# Revit family: HV1 für Kältefestpunkt_
name_source: partatom
category: Allgemeines Modell
revit_build: Autodesk Revit 2017 (Build: 20190508_0315(x64)
units: mm (PartAtom-declared; Revit-internal decimal feet)

## family parameters
Basisbauteil = Fläche
Beim Laden mit Abzugskörper schneiden = Nein
Bemaßung runder Anschluss = Durchmesser verwenden
Gemeinsam genutzt = Ja
Kann Basisbauteil für Bewehrung sein = Nein
Raumberechnungspunkt = Nein
Teiletyp = Normal

## types (5) — shared parameters
Anzahl Rohrschellen = 2
Anzugsmoment Hammersperrkopf = 120 Nm
Artikelnummer = 00200405/fvz
Breite Material Rohrschelle = 50 mm
EAN = 4250928400000
Fabrikat = MEFA
Gewicht = 3.58 kg
Kurztext1 = Festpunkthalterung HV 1
Kurztext2 = 64 - 273 mm Fx 20 kN 111 - 163 mm
Länge = 120 mm  [stored 0.393701 ft]
Mengeneinheit = St
Rohrschellentyp = Titan HD
Stärke Material Rohrschelle = 5 mm
Vorgabe-Ansicht = 1219 mm
max. Achshöhe = 163 mm
max. Rohraußendurchmesser = 273 mm  [stored 0.895669 ft]
max. zul. Last Fx = 4.50 kip
max. zul. Last Fz = 2.70 kip
min. Achshöhe = 111 mm
min. Rohraußendurchmesser = 64 mm  [stored 0.209974 ft]
vpe = 1

## per-type parameters (varying)
| type | S |
| HV1 für Kältefestpunkt Ø76,1 mm | 206 mm |
| HV1 für Kältefestpunkt Ø88,9 mm | 217 mm  [stored 0.711942 ft] |
| HV1 für Kältefestpunkt Ø114,3 mm | 243 mm |
| HV1 für Kältefestpunkt Ø139,7 mm | 271 mm |
| HV1 für Kältefestpunkt Ø168,3 mm | 299 mm |

note: [stored X ft] marks values corroborated as IEEE doubles in the binary element streams (Revit-internal decimal feet)

## geometry (parser evidence)
native form markers: Sweep x9
no freeform markers — native parametric forms only
